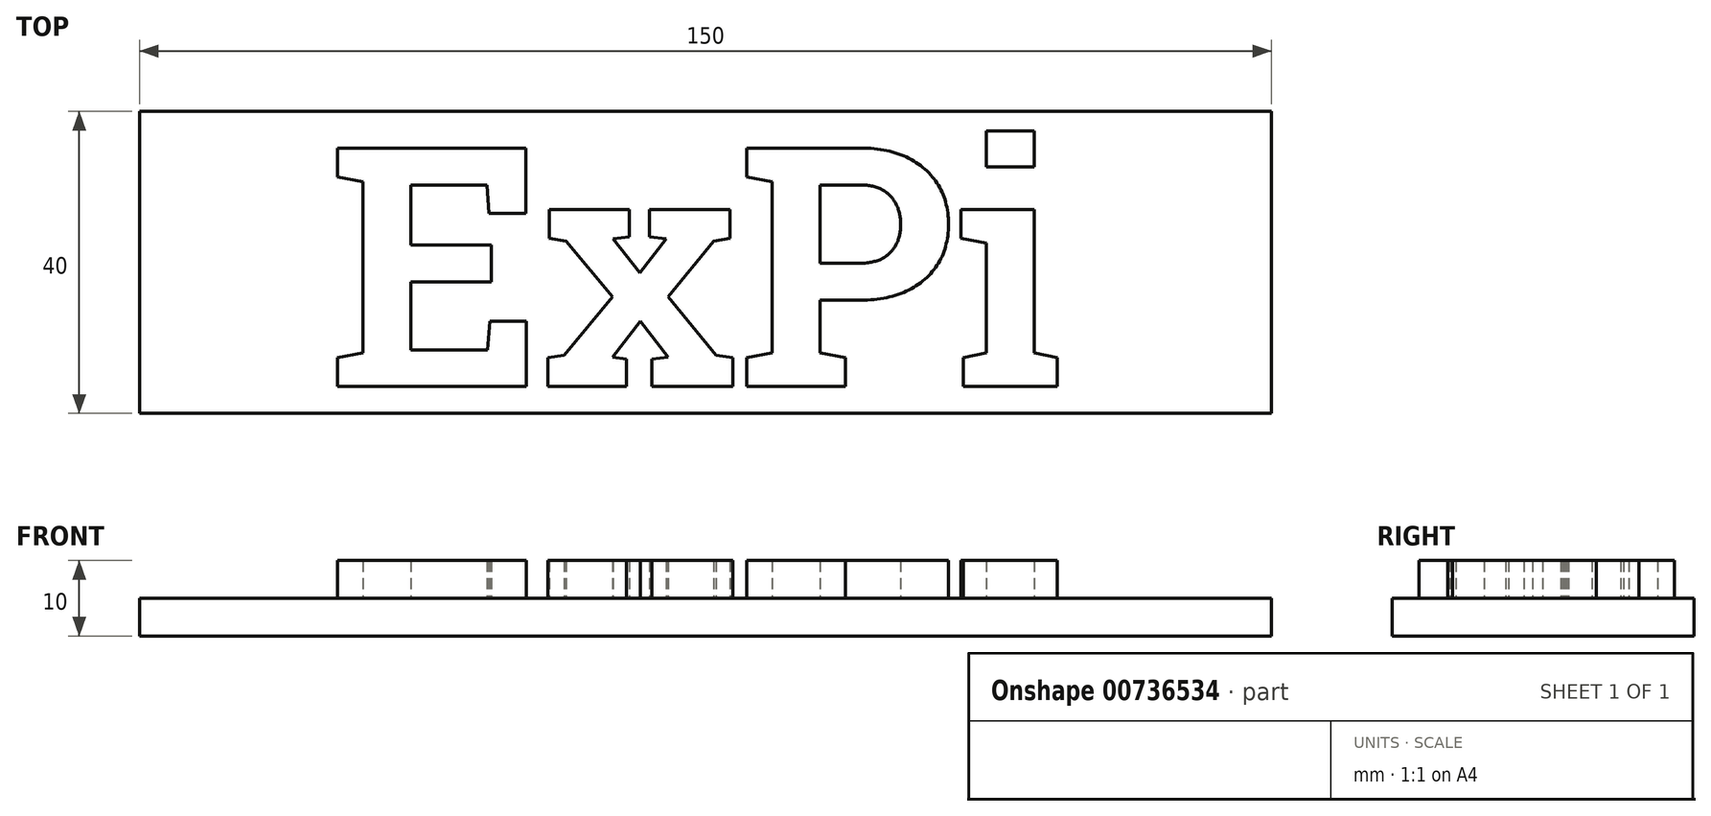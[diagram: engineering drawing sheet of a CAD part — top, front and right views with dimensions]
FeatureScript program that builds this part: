
annotation { "Feature Type Name" : "Feature", "Feature Type Description" : "" }
export const myFeature = defineFeature(function(context is Context, id is Id, definition is map)
    precondition{}
    {
        {
            var Q0;
            Q0=qCreatedBy(makeId("Top.planeOp"),FACE);
            var sketch = newSketch(context, id + "F0", { "sketchPlane" : qUnion([Q0])});
            skLineSegment(sketch, "E0.bottom", {"start": v(75, 20) * mm, "end": v(-75, 20) * mm});
            skLineSegment(sketch, "E0.top", {"start": v(75, -20) * mm, "end": v(-75, -20) * mm});
            skLineSegment(sketch, "E0.left", {"start": v(75, 20) * mm, "end": v(75, -20) * mm});
            skLineSegment(sketch, "E0.right", {"start": v(-75, 20) * mm, "end": v(-75, -20) * mm});
            skPoint(sketch, "E0.middle", {"position": v(0, 0) * mm});
            skSolve(sketch);
        }
        {
            var Q0;
            Q0=makeQuery(id+"F0.imprint","IMPRINT",FACE,{"disambiguationData":[TD([[makeQuery(id+"F0.imprint","IMPRINT",EDGE,{"derivedFrom":sQuery(id+"F0.wireOp",EDGE,"E0.bottom")}),1.0]])]});
            extrude(context, id + "F1", {"entities" : qUnion([Q0]), "depth" : 5 * mm, "offsetDistance" : 25 * mm});
        }
        {
            var Q0;
            Q0=makeQuery(id+"F1.opExtrude","CAP_FACE",FACE,{"disambiguationData":[OSD([sQuery(id+"F0.wireOp",EDGE,"E0.bottom"),sQuery(id+"F0.wireOp",EDGE,"E0.top"),sQuery(id+"F0.wireOp",EDGE,"E0.left"),sQuery(id+"F0.wireOp",EDGE,"E0.right")])],"isStart":false});
            var sketch = newSketch(context, id + "F2", { "sketchPlane" : qUnion([Q0])});
            skText(sketch, "E1", { "text": "ExPi\n", "fontName": "RobotoSlab-Bold.ttf"});
            const initialGuessF2  = {"E1": [-0.05, -0.01645, 1, 0, 0.032]};
            skSetInitialGuess(sketch, initialGuessF2);
            skSolve(sketch);
        }
        {
            var Q0;
            Q0 = qSketchRegion(id + "F2", true);
            extrude(context, id + "F3", {"entities" : qUnion([Q0]), "operationType" : NewBodyOperationType.ADD, "depth" : 5 * mm, "offsetDistance" : 25 * mm});
        }
    });
